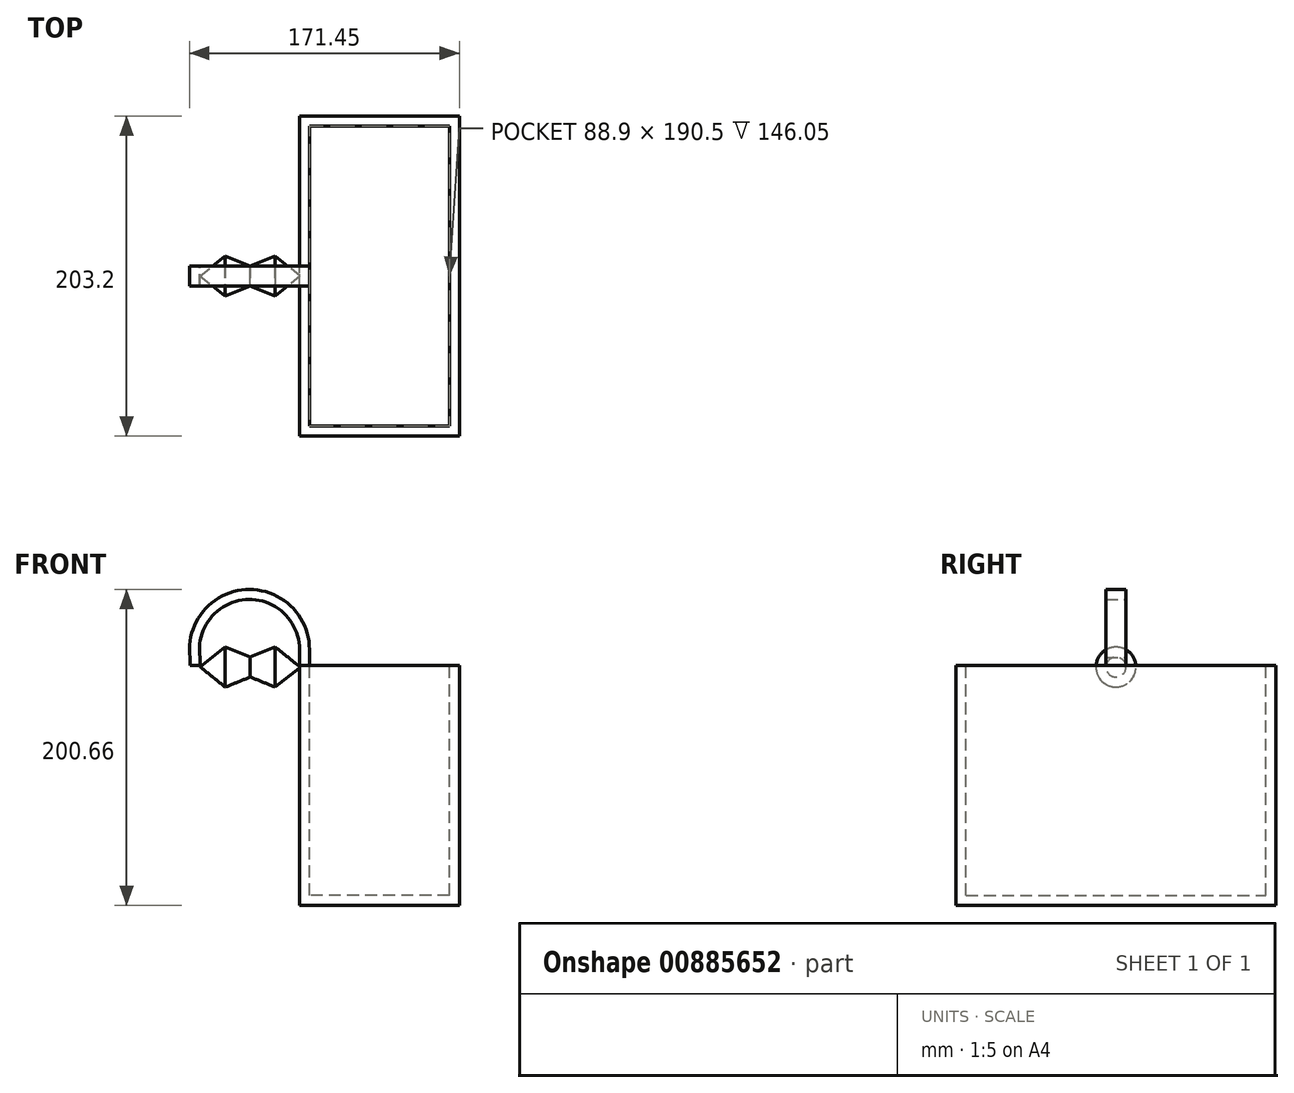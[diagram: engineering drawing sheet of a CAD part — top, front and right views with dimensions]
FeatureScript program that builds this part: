
annotation { "Feature Type Name" : "Feature", "Feature Type Description" : "" }
export const myFeature = defineFeature(function(context is Context, id is Id, definition is map)
    precondition{}
    {
        {
            var Q0;
            Q0=qCreatedBy(makeId("Front.planeOp"),FACE);
            var sketch = newSketch(context, id + "F0", { "sketchPlane" : qUnion([Q0])});
            skLineSegment(sketch, "E0.bottom", {"start": v(0, 0) * mm, "end": v(-101.6, 0) * mm});
            skLineSegment(sketch, "E0.top", {"start": v(0, 152.4) * mm, "end": v(-101.6, 152.4) * mm});
            skLineSegment(sketch, "E0.left", {"start": v(0, 0) * mm, "end": v(0, 152.4) * mm});
            skLineSegment(sketch, "E0.right", {"start": v(-101.6, 0) * mm, "end": v(-101.6, 152.4) * mm});
            skSolve(sketch);
        }
        {
            var Q0;
            Q0 = qSketchRegion(id + "F0", true);
            extrude(context, id + "F1", {"entities" : qUnion([Q0]), "depth" : 101.6 * mm, "offsetDistance" : 25.4 * mm});
        }
        {
            var Q0;
            Q0=makeQuery(id+"F1.opExtrude","SWEPT_FACE",FACE,{"disambiguationData":[OSD([sQuery(id+"F0.wireOp",EDGE,"E0.top")])]});
            var Q1;
            Q1=makeQuery(id+"F1.opExtrude","CAP_FACE",FACE,{"disambiguationData":[OSD([sQuery(id+"F0.wireOp",EDGE,"E0.bottom"),sQuery(id+"F0.wireOp",EDGE,"E0.top"),sQuery(id+"F0.wireOp",EDGE,"E0.left"),sQuery(id+"F0.wireOp",EDGE,"E0.right")])],"isStart":true});
            shell(context, id + "F2", {"entities" : qUnion([Q0, Q1]), "thickness" : 6.35 * mm});
        }
        {
            var Q0;
            Q0=makeQuery(id+"F1.opExtrude","CAP_FACE",FACE,{"disambiguationData":[OSD([sQuery(id+"F0.wireOp",EDGE,"E0.bottom"),sQuery(id+"F0.wireOp",EDGE,"E0.top"),sQuery(id+"F0.wireOp",EDGE,"E0.left"),sQuery(id+"F0.wireOp",EDGE,"E0.right")])],"isStart":true});
            var sketch = newSketch(context, id + "F3", { "sketchPlane" : qUnion([Q0])});
            skLineSegment(sketch, "E1", {"start": v(101.6, 152.4) * mm, "end": v(101.6, 162.56) * mm});
            skArc(sketch, "E2", {"start": v(164.7, 157.48) * mm, "mid": v(135.9, 194.2) * mm, "end": v(101.6, 162.56) * mm});
            skLineSegment(sketch, "E3", {"start": v(95.25, 152.4) * mm, "end": v(95.25, 162.56) * mm});
            skArc(sketch, "E4", {"start": v(171.1, 157.48) * mm, "mid": v(135.9, 200.57) * mm, "end": v(95.25, 162.56) * mm});
            skLineSegment(sketch, "E5.top", {"start": v(171.1, 152.4) * mm, "end": v(164.7, 152.4) * mm});
            skLineSegment(sketch, "E5.left", {"start": v(171.1, 157.48) * mm, "end": v(171.1, 152.4) * mm});
            skLineSegment(sketch, "E5.right", {"start": v(164.7, 157.48) * mm, "end": v(164.7, 152.4) * mm});
            skSolve(sketch);
        }
        {
            var Q0;
            Q0=makeQuery(id+"F3.imprint","IMPRINT",FACE,{"disambiguationData":[TD([[makeQuery(id+"F3.imprint","IMPRINT",EDGE,{"derivedFrom":sQuery(id+"F3.wireOp",EDGE,"E1")}),1.0]])]});
            extrude(context, id + "F4", {"entities" : qUnion([Q0]), "operationType" : NewBodyOperationType.ADD, "oppositeDirection" : true, "depth" : 6.35 * mm, "offsetDistance" : 25.4 * mm});
        }
        {
            var Q0;
            Q0=makeQuery(id+"F1.opExtrude","SWEPT_BODY",BODY,{"disambiguationData":[OSD([sQuery(id+"F0.wireOp",EDGE,"E0.bottom"),sQuery(id+"F0.wireOp",EDGE,"E0.top"),sQuery(id+"F0.wireOp",EDGE,"E0.left"),sQuery(id+"F0.wireOp",EDGE,"E0.right")])]});
            var Q1;
            Q1=makeQuery(id+"F1.opExtrude","CAP_FACE",FACE,{"disambiguationData":[OSD([sQuery(id+"F0.wireOp",EDGE,"E0.bottom"),sQuery(id+"F0.wireOp",EDGE,"E0.top"),sQuery(id+"F0.wireOp",EDGE,"E0.left"),sQuery(id+"F0.wireOp",EDGE,"E0.right")])],"isStart":true});
            mirror(context, id + "F5", {"operationType" : NewBodyOperationType.ADD, "entities" : qUnion([Q0]), "mirrorPlane" : qUnion([Q1])});
        }
        {
            var Q0;
            Q0=qCreatedBy(makeId("Front.planeOp"),FACE);
            var sketch = newSketch(context, id + "F6", { "sketchPlane" : qUnion([Q0])});
            skLineSegment(sketch, "E6", {"start": v(0, 0) * mm, "end": v(63.5, 0) * mm});
            skLineSegment(sketch, "E7", {"start": v(63.5, 0) * mm, "end": v(47.62, -12.7) * mm});
            skLineSegment(sketch, "E8", {"start": v(47.62, -12.7) * mm, "end": v(31.75, -6.35) * mm});
            skLineSegment(sketch, "E9", {"start": v(31.75, -6.35) * mm, "end": v(15.87, -12.7) * mm});
            skLineSegment(sketch, "E10", {"start": v(15.87, -12.7) * mm, "end": v(0, 0) * mm});
            skSolve(sketch);
        }
        {
            var Q0;
            Q0=qCreatedBy(makeId("Right.planeOp"),FACE);
            var sketch = newSketch(context, id + "F7", { "sketchPlane" : qUnion([Q0])});
            skCircle(sketch, "E11", {"center": v(0, 0) * mm, "radius": 4.6 * mm});
            skSolve(sketch);
        }
        {
            var Q0;
            Q0=makeQuery(id+"F6.imprint","IMPRINT",FACE,{"disambiguationData":[TD([[makeQuery(id+"F6.imprint","IMPRINT",EDGE,{"derivedFrom":sQuery(id+"F6.wireOp",EDGE,"E6")}),-1.0]])]});
            var Q1;
            Q1=sQuery(id+"F7.wireOp",EDGE,"E11");
            sweep(context, id + "F8", {"profiles" : qUnion([Q0]), "path" : qUnion([Q1])});
        }
        {
            var Q0;
            Q0=makeQuery(id+"F8.opSweep","SWEPT_BODY",BODY,{"disambiguationData":[OSD([sQuery(id+"F6.wireOp",EDGE,"CPL6dcom-h0M8-xlFC-2n2t-0j2Vaj4pYUdL"),sQuery(id+"F6.wireOp",EDGE,"vkPnHQi5-VlvS-4pwr-BMPC-lUpZbeB6k9AZ"),sQuery(id+"F6.wireOp",EDGE,"ZKlvxbob-6yXH-XbgL-xtRx-GhPK1yPMotqY"),sQuery(id+"F6.wireOp",EDGE,"Dlycq66e-IEDL-hHvN-f9ln-V6Il464QVMw3"),sQuery(id+"F6.wireOp",EDGE,"E6"),sQuery(id+"F7.wireOp",EDGE,"E11")])]});
            transform(context, id + "F9", {"entities" : qUnion([Q0]), "transformType" : TransformType.TRANSLATION_3D, "dx" : -164.6 * mm, "dy" : 0 * mm, "dz" : 151.38 * mm, "makeCopy" : false});
        }
    });
